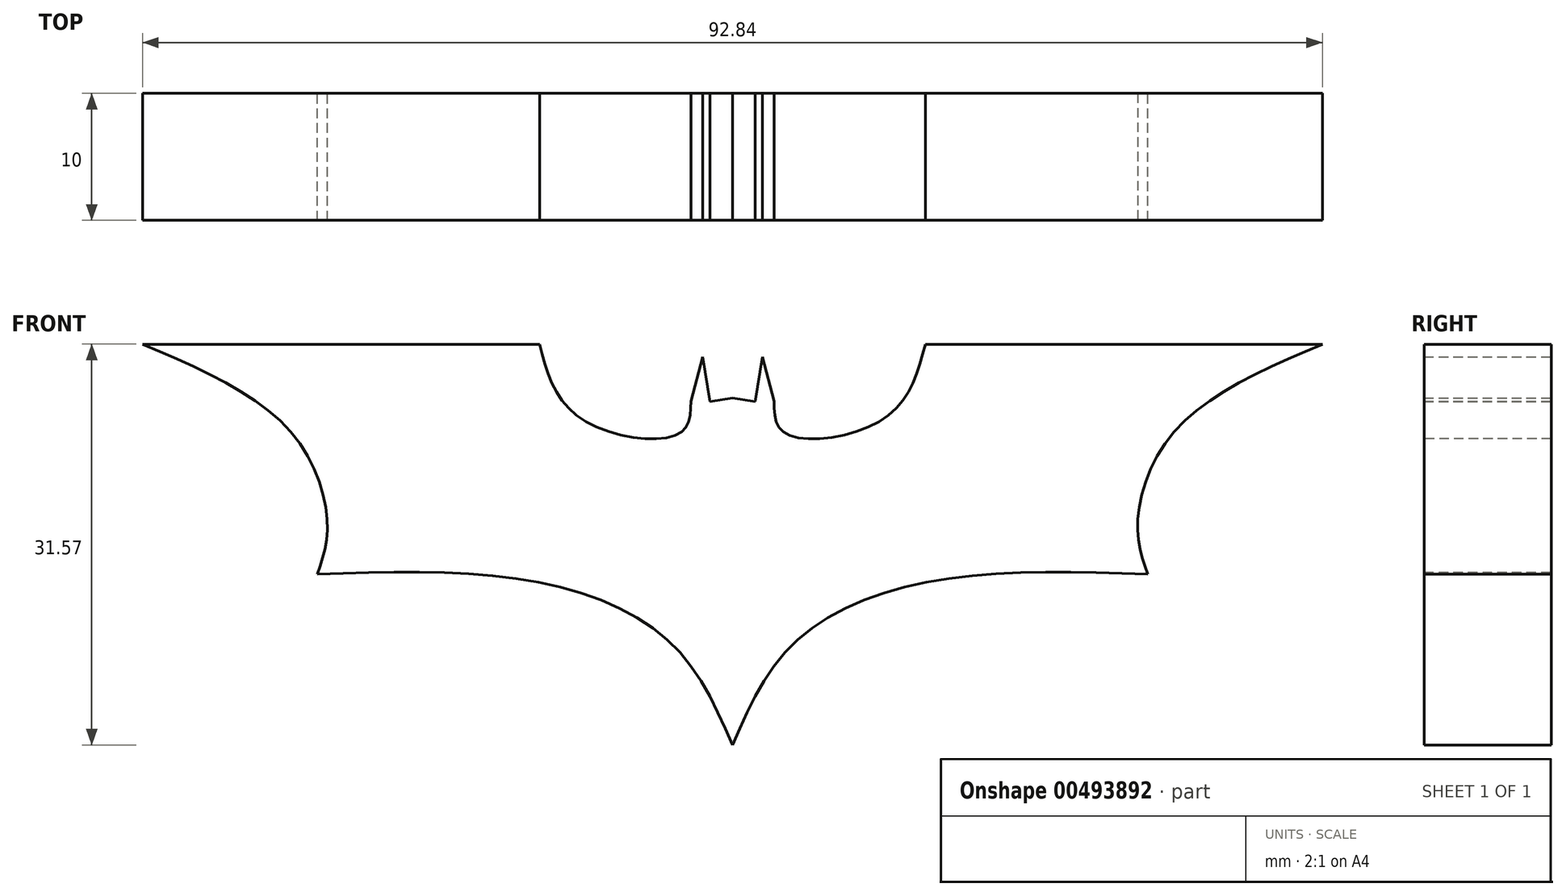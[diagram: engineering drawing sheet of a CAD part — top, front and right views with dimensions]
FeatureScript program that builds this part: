
annotation { "Feature Type Name" : "Feature", "Feature Type Description" : "" }
export const myFeature = defineFeature(function(context is Context, id is Id, definition is map)
    precondition{}
    {
        {
            var Q0;
            Q0=qCreatedBy(makeId("Front.planeOp"),FACE);
            var sketch = newSketch(context, id + "F0", { "sketchPlane" : qUnion([Q0])});
            skLineSegment(sketch, "E0", {"start": v(0, 0) * mm, "end": v(0, 32.12) * mm});
            skLineSegment(sketch, "E1", {"start": v(0, 32.12) * mm, "end": v(0, 27.34) * mm});
            skLineSegment(sketch, "E2", {"start": v(0, 27.34) * mm, "end": v(1.78, 27.05) * mm});
            skLineSegment(sketch, "E3", {"start": v(1.78, 27.05) * mm, "end": v(2.35, 30.55) * mm});
            skLineSegment(sketch, "E4", {"start": v(2.35, 30.55) * mm, "end": v(3.28, 27.09) * mm});
            skFitSpline(sketch, "E5", {"points": [v(3.28, 27.09) * mm, v(4.19, 24.53) * mm, v(11.96, 25.73) * mm, v(15.18, 31.57) * mm], "startDerivative": vector(0.16, -13.06) * mm, "endDerivative": vector(4.68, 18.1) * mm});
            skLineSegment(sketch, "E6", {"start": v(15.18, 31.57) * mm, "end": v(46.42, 31.57) * mm});
            skFitSpline(sketch, "E7", {"points": [v(46.42, 31.57) * mm, v(34.75, 24.66) * mm, v(31.87, 17.22) * mm, v(32.67, 13.47) * mm], "startDerivative": vector(-31.24, -13.4) * mm, "endDerivative": vector(5.26, -14.58) * mm});
            skFitSpline(sketch, "E8", {"points": [v(32.67, 13.47) * mm, v(15.11, 12.8) * mm, v(4.65, 7.84) * mm, v(0, 0) * mm], "startDerivative": vector(-46.67, 1.4) * mm, "endDerivative": vector(-12.96, -29.8) * mm});
            skFitSpline(sketch, "E9.MirrorCS", {"points": [v(-46.42, 31.57) * mm, v(-34.75, 24.66) * mm, v(-31.87, 17.22) * mm, v(-32.67, 13.47) * mm], "startDerivative": vector(31.24, -13.4) * mm, "endDerivative": vector(-5.26, -14.58) * mm});
            skLineSegment(sketch, "E10.MirrorCS", {"start": v(-15.18, 31.57) * mm, "end": v(-46.42, 31.57) * mm});
            skLineSegment(sketch, "E11.MirrorCS", {"start": v(-1.78, 27.05) * mm, "end": v(-2.35, 30.55) * mm});
            skFitSpline(sketch, "E12.MirrorCS", {"points": [v(-3.28, 27.09) * mm, v(-4.19, 24.53) * mm, v(-11.96, 25.73) * mm, v(-15.18, 31.57) * mm], "startDerivative": vector(-0.16, -13.06) * mm, "endDerivative": vector(-4.68, 18.1) * mm});
            skLineSegment(sketch, "E13.MirrorCS", {"start": v(-2.35, 30.55) * mm, "end": v(-3.28, 27.09) * mm});
            skFitSpline(sketch, "E14.MirrorCS", {"points": [v(-3.28, 27.09) * mm, v(-4.19, 24.53) * mm, v(-11.96, 25.73) * mm, v(-15.18, 31.57) * mm], "startDerivative": vector(-0.16, -13.06) * mm, "endDerivative": vector(-4.68, 18.1) * mm});
            skFitSpline(sketch, "E15.MirrorCS", {"points": [v(-32.67, 13.47) * mm, v(-15.11, 12.8) * mm, v(-4.65, 7.84) * mm, v(0, 0) * mm], "startDerivative": vector(46.67, 1.4) * mm, "endDerivative": vector(12.96, -29.8) * mm});
            skLineSegment(sketch, "E16", {"start": v(-1.78, 27.05) * mm, "end": v(0, 27.34) * mm});
            skSolve(sketch);
        }
        {
            var Q0;
            Q0=makeQuery(id+"F0.imprint","IMPRINT",FACE,{"disambiguationData":[TD([[makeQuery(id+"F0.imprint","IMPRINT",EDGE,{"derivedFrom":sQuery(id+"F0.wireOp",EDGE,"E0")}),1.0]])]});
            var Q1;
            Q1=makeQuery(id+"F0.imprint","IMPRINT",FACE,{"disambiguationData":[TD([[makeQuery(id+"F0.imprint","IMPRINT",EDGE,{"derivedFrom":sQuery(id+"F0.wireOp",EDGE,"E0")}),-1.0]])]});
            var Q2;
            Q2=sQuery(id+"F0.wireOp",EDGE,"E15.MirrorCS");
            var Q3;
            Q3=sQuery(id+"F0.wireOp",EDGE,"E0");
            var Q4;
            Q4=sQuery(id+"F0.wireOp",EDGE,"E5");
            var Q5;
            Q5=sQuery(id+"F0.wireOp",EDGE,"E6");
            var Q6;
            Q6=sQuery(id+"F0.wireOp",EDGE,"E7");
            var Q7;
            Q7=sQuery(id+"F0.wireOp",EDGE,"E8");
            var Q8;
            Q8=sQuery(id+"F0.wireOp",EDGE,"E9.MirrorCS");
            var Q9;
            Q9=sQuery(id+"F0.wireOp",EDGE,"E10.MirrorCS");
            var Q10;
            Q10=sQuery(id+"F0.wireOp",EDGE,"E12.MirrorCS");
            var Q11;
            Q11=sQuery(id+"F0.wireOp",EDGE,"E9.MirrorCS");
            var Q12;
            Q12=sQuery(id+"F0.wireOp",EDGE,"E10.MirrorCS");
            var Q13;
            Q13=sQuery(id+"F0.wireOp",EDGE,"E12.MirrorCS");
            var Q14;
            Q14=sQuery(id+"F0.wireOp",EDGE,"E9.MirrorCS");
            var Q15;
            Q15=sQuery(id+"F0.wireOp",EDGE,"E10.MirrorCS");
            var Q16;
            Q16=sQuery(id+"F0.wireOp",EDGE,"E14.MirrorCS");
            var Q17;
            Q17=sQuery(id+"F0.wireOp",EDGE,"E1");
            var Q18;
            Q18=sQuery(id+"F0.wireOp",EDGE,"E4");
            var Q19;
            Q19=sQuery(id+"F0.wireOp",EDGE,"E2");
            var Q20;
            Q20=sQuery(id+"F0.wireOp",EDGE,"E3");
            var Q21;
            Q21=sQuery(id+"F0.wireOp",EDGE,"E16");
            var Q22;
            Q22=sQuery(id+"F0.wireOp",EDGE,"E13.MirrorCS");
            var Q23;
            Q23=sQuery(id+"F0.wireOp",EDGE,"E11.MirrorCS");
            var Q24;
            Q24=sQuery(id+"F0.wireOp",EDGE,"E13.MirrorCS");
            var Q25;
            Q25=sQuery(id+"F0.wireOp",EDGE,"E11.MirrorCS");
            var Q26;
            Q26=sQuery(id+"F0.wireOp",EDGE,"E13.MirrorCS");
            var Q27;
            Q27=sQuery(id+"F0.wireOp",EDGE,"E11.MirrorCS");
            extrude(context, id + "F1", {"entities" : qUnion([Q0, Q1]), "surfaceEntities" : qUnion([Q2, Q3, Q4, Q5, Q6, Q7, Q8, Q9, Q10, Q11, Q12, Q13, Q14, Q15, Q16, Q17, Q18, Q19, Q20, Q21, Q22, Q23, Q24, Q25, Q26, Q27]), "depth" : 10 * mm});
        }
    });
